# Revit family: NLRS_57_DUA_UN_connection sleeve for penthouse louvre LT_sacs
name_source: partatom
category: Duct Accessories
revit_build: Autodesk Revit 2018 (Build: 20190510_1515(x64)
units: mm (PartAtom-declared; Revit-internal decimal feet)

## family parameters
Always vertical = Yes
Cut with Voids When Loaded = No
Part Type = Attaches To
Round Connector Dimension = Use Diameter
Shared = Yes
Work Plane-Based = No

## types (2) — shared parameters
Assembly Code = 57.0
LookupTable = BDOK
Manufacturer = Solid Air Climate Solutions
Model = Solid Air roof curb, BDOK
NLRS_C_content_datum_uitgifte = 22-04-2021
NLRS_C_content_provider = Solid Air Climate Solutions
NLRS_C_content_versie = 3.18.01
NLRS_C_niveau ontwikkeling = LOD 400

## per-type parameters (varying)
| type | Description | NLRS_C_description | SACS_Base_Index | SACS_Face_Color | SACS_Frame_1 | SACS_Frame_2 | SACS_Material |
| BDOKOO | Galvanised steel connection sleeve | Galvanised steel connection sleeve | 1 | NLRS_57_sendzimir verzinkt_gen_sacs | Yes | No | galvanised steel |
| BDOKAO | Aluminium connection sleeve | Aluminium connection sleeve | 2 | NLRS_57_aluminium_gen_sacs | No | Yes | seawater proof aluminium |

## geometry (parser evidence)
native form markers: Sweep x6
no freeform markers — native parametric forms only
